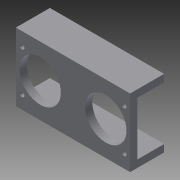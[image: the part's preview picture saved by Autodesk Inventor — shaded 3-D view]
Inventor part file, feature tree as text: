
AUTODESK INVENTOR PART (.ipt)
format: ipt  version: 2015 (Build 190159000, 159)  size: 142,336 bytes
history: native  units: in
note: dims shown in document units (in); Inventor stores cm internally (conversion verified against a paired STEP export)
features: reference x16, extrude x5, sketch x5
ambient origin geometry x8: Origin, YZ Plane, XZ Plane, XY Plane, X Axis, Y Axis, Z Axis, Center Point
bodies: Solid1 (feature_tree)
feature tree (26):
  extrude  "Extrusion1"  Depth=1.8504in
  extrude  "Extrusion2"  Depth=0.0394in
  extrude  "Extrusion3"  Depth=0.0394in
  extrude  "Extrusion4"  Depth=0.1181in
  extrude  "Extrusion5"  Depth=0.8661in
  sketch  "Sketch1"  dims[d0=0.6693in d1=1.8504in]
  reference  "Reference1"
  reference  "Reference2"
  reference  "Reference3"
  reference  "Reference4"
  reference  "Reference5"
  reference  "Reference6"
  reference  "Reference7"
  reference  "Reference8"
  reference  "Reference9"
  reference  "Reference10"
  reference  "Reference11"
  reference  "Reference12"
  sketch  "Sketch5"  dims[d2=0.8661in d3=0.0394in]
  sketch  "Sketch6"  dims[d4=0.0394in d5=0.6693in]
  reference  "Reference14"
  reference  "Reference15"
  reference  "Reference16"
  reference  "Reference17"
  sketch  "Sketch8"  dims[d6=0.1181in d7=0.0in d12=0.1181in]
  sketch  "Sketch9"  dims[d14=0.1181in d15=0.8661in d16=1.8504in d17=0.0in d18=0.1969in d19=0.1969in d20=0.1969in d21=1.8504in d22=0.0in d23=0.1181in d24=0.0in d25=0.1181in d26=0.0in]
